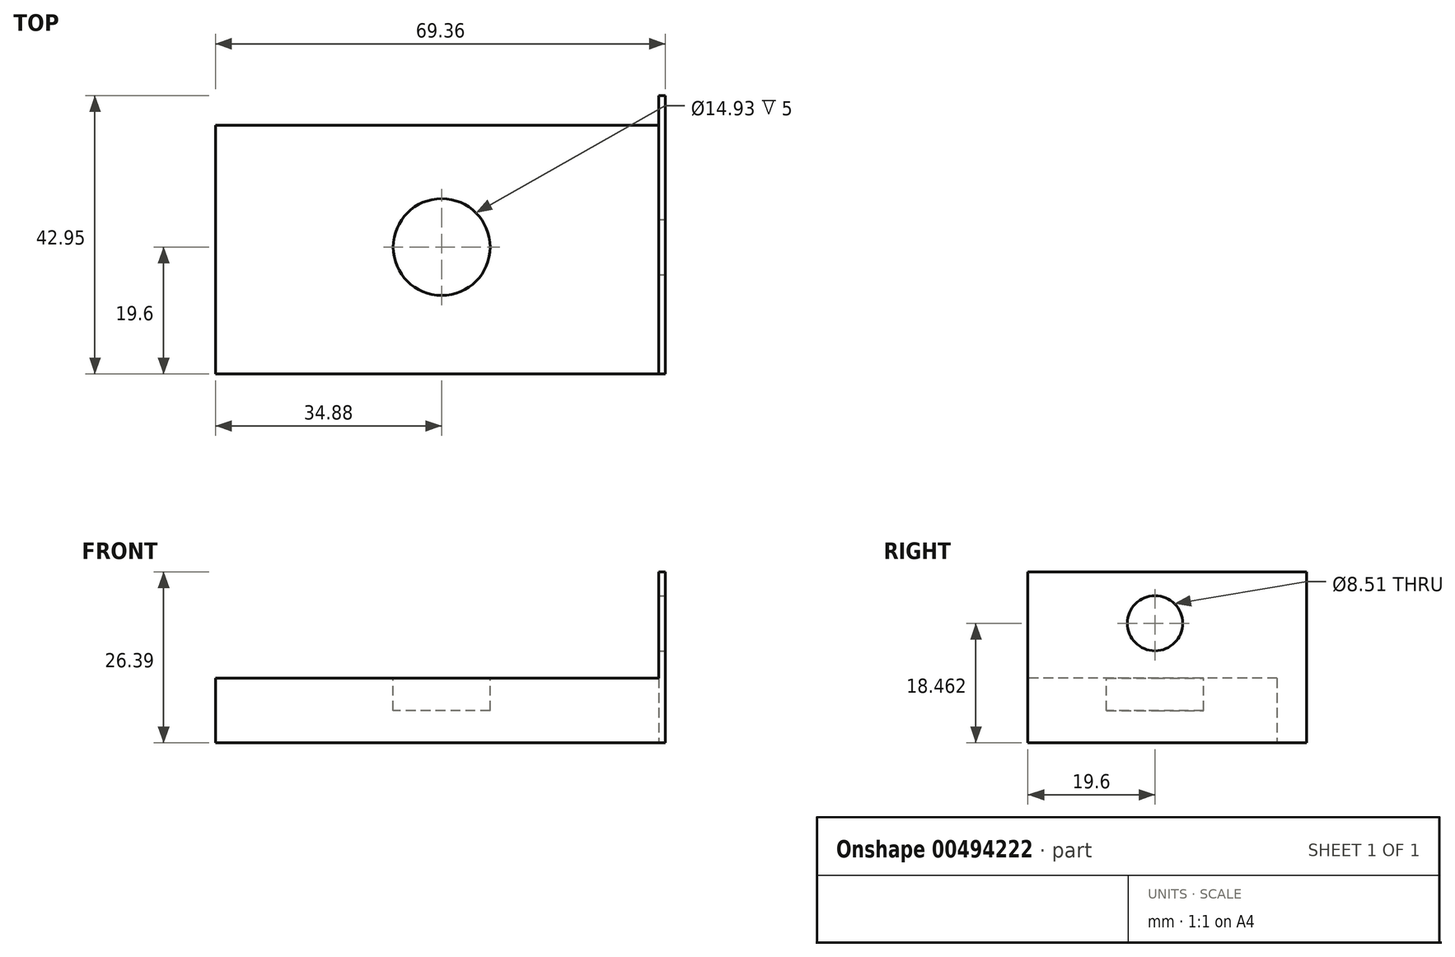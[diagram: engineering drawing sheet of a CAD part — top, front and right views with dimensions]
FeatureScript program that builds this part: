
annotation { "Feature Type Name" : "Feature", "Feature Type Description" : "" }
export const myFeature = defineFeature(function(context is Context, id is Id, definition is map)
    precondition{}
    {
        {
            var Q0;
            Q0=qCreatedBy(makeId("Top.planeOp"),FACE);
            var sketch = newSketch(context, id + "F0", { "sketchPlane" : qUnion([Q0])});
            skLineSegment(sketch, "E0.bottom", {"start": v(-34.88, 18.8) * mm, "end": v(33.48, 18.8) * mm});
            skLineSegment(sketch, "E0.top", {"start": v(-34.88, -19.6) * mm, "end": v(33.48, -19.6) * mm});
            skLineSegment(sketch, "E0.left", {"start": v(-34.88, 18.8) * mm, "end": v(-34.88, -19.6) * mm});
            skLineSegment(sketch, "E0.right", {"start": v(33.48, 18.8) * mm, "end": v(33.48, -19.6) * mm});
            skSolve(sketch);
        }
        {
            var Q0;
            Q0 = qSketchRegion(id + "F0", true);
            extrude(context, id + "F1", {"entities" : qUnion([Q0]), "depth" : 10 * mm});
        }
        {
            var Q0;
            Q0=makeQuery(id+"F1.opExtrude","CAP_FACE",FACE,{"disambiguationData":[OSD([sQuery(id+"F0.wireOp",EDGE,"E0.bottom"),sQuery(id+"F0.wireOp",EDGE,"E0.top"),sQuery(id+"F0.wireOp",EDGE,"E0.left"),sQuery(id+"F0.wireOp",EDGE,"E0.right")])],"isStart":false});
            var sketch = newSketch(context, id + "F2", { "sketchPlane" : qUnion([Q0])});
            skCircle(sketch, "E1", {"center": v(0, 0) * mm, "radius": 7.47 * mm});
            skSolve(sketch);
        }
        {
            var Q0;
            Q0 = qSketchRegion(id + "F2", true);
            extrude(context, id + "F3", {"entities" : qUnion([Q0]), "operationType" : NewBodyOperationType.REMOVE, "oppositeDirection" : true, "depth" : 5 * mm});
        }
        {
            var Q0;
            Q0=makeQuery(id+"F1.opExtrude","SWEPT_FACE",FACE,{"disambiguationData":[OSD([sQuery(id+"F0.wireOp",EDGE,"E0.right")])]});
            var sketch = newSketch(context, id + "F4", { "sketchPlane" : qUnion([Q0])});
            skLineSegment(sketch, "E2.bottom", {"start": v(-19.6, 0) * mm, "end": v(23.35, 0) * mm});
            skLineSegment(sketch, "E2.top", {"start": v(-19.6, 26.39) * mm, "end": v(23.35, 26.39) * mm});
            skLineSegment(sketch, "E2.left", {"start": v(-19.6, 0) * mm, "end": v(-19.6, 26.39) * mm});
            skLineSegment(sketch, "E2.right", {"start": v(23.35, 0) * mm, "end": v(23.35, 26.39) * mm});
            skSolve(sketch);
        }
        {
            var Q0;
            Q0 = qSketchRegion(id + "F4", true);
            extrude(context, id + "F5", {"entities" : qUnion([Q0]), "operationType" : NewBodyOperationType.ADD, "depth" : 1 * mm});
        }
        {
            var Q0;
            Q0=makeQuery(id+"F5.opExtrude","CAP_FACE",FACE,{"disambiguationData":[OSD([sQuery(id+"F4.wireOp",EDGE,"E2.bottom"),sQuery(id+"F4.wireOp",EDGE,"E2.top"),sQuery(id+"F4.wireOp",EDGE,"E2.left"),sQuery(id+"F4.wireOp",EDGE,"E2.right")])],"isStart":false});
            var sketch = newSketch(context, id + "F6", { "sketchPlane" : qUnion([Q0])});
            skCircle(sketch, "E3", {"center": v(0, 18.46) * mm, "radius": 4.25 * mm});
            skSolve(sketch);
        }
        {
            var Q0;
            Q0 = qSketchRegion(id + "F6", true);
            extrude(context, id + "F7", {"entities" : qUnion([Q0]), "operationType" : NewBodyOperationType.REMOVE, "oppositeDirection" : true, "depth" : 1 * mm});
        }
    });
